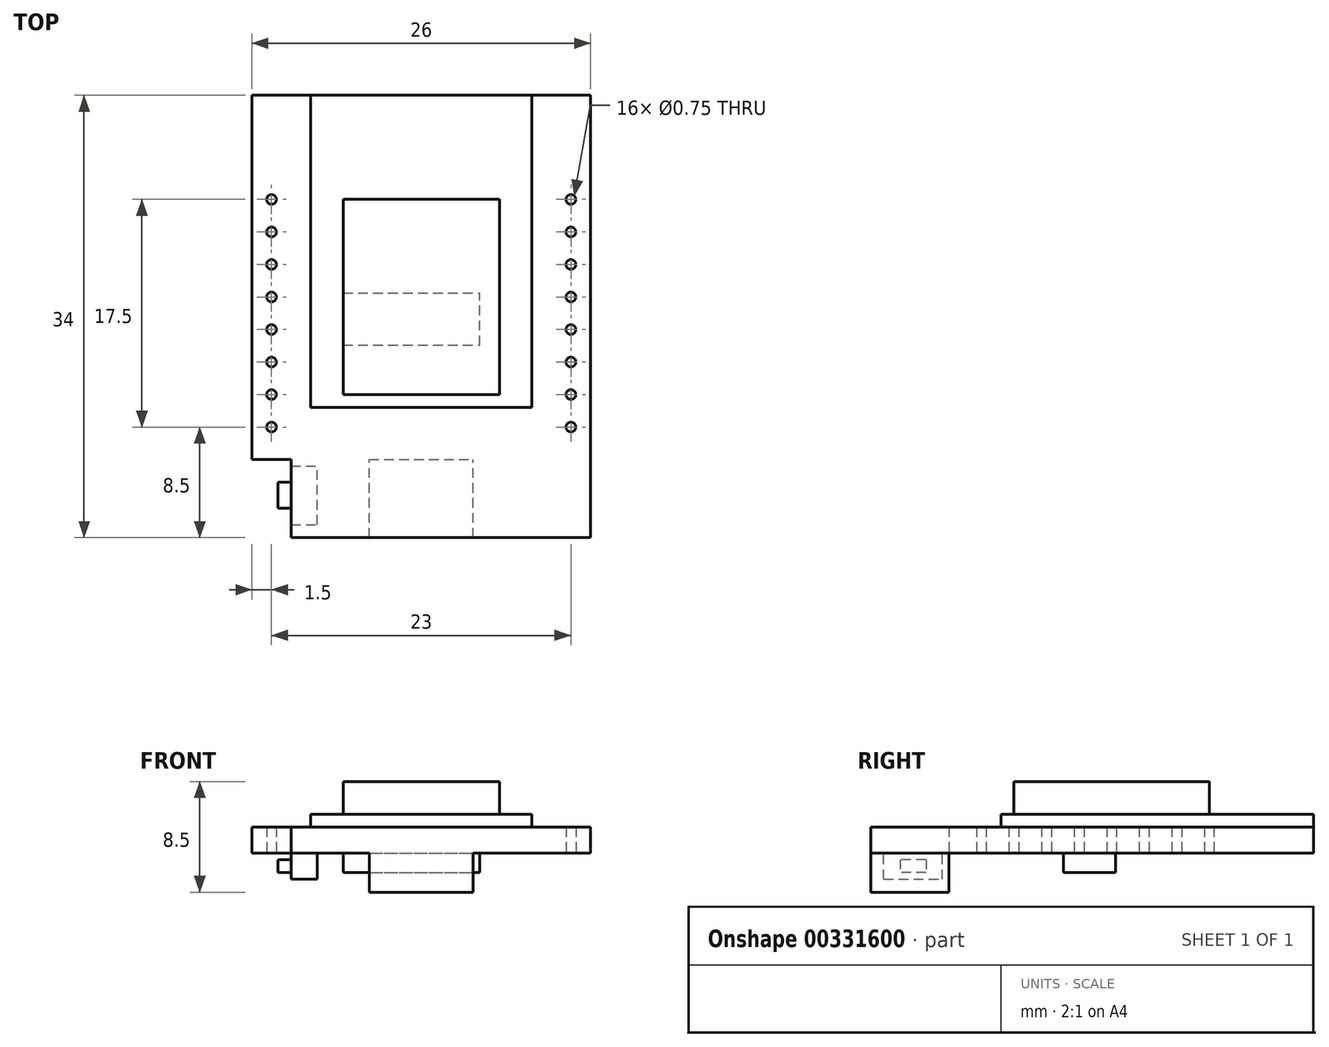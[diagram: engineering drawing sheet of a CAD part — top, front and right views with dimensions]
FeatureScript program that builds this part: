
annotation { "Feature Type Name" : "Feature", "Feature Type Description" : "" }
export const myFeature = defineFeature(function(context is Context, id is Id, definition is map)
    precondition{}
    {
        {
            var Q0;
            Q0=qCreatedBy(makeId("Top.planeOp"),FACE);
            var sketch = newSketch(context, id + "F0", { "sketchPlane" : qUnion([Q0])});
            skLineSegment(sketch, "E0.bottom", {"start": v(-13, 17) * mm, "end": v(13, 17) * mm});
            skLineSegment(sketch, "E0.top", {"start": v(-10, -17) * mm, "end": v(13, -17) * mm});
            skLineSegment(sketch, "E0.left", {"start": v(-13, 17) * mm, "end": v(-13, -11) * mm});
            skLineSegment(sketch, "E0.right", {"start": v(13, 17) * mm, "end": v(13, -17) * mm});
            skLineSegment(sketch, "E1.top", {"start": v(-13, -11) * mm, "end": v(-10, -11) * mm});
            skLineSegment(sketch, "E1.right", {"start": v(-10, -17) * mm, "end": v(-10, -11) * mm});
            skSolve(sketch);
        }
        {
            var Q0;
            Q0 = qSketchRegion(id + "F0", true);
            extrude(context, id + "F1", {"entities" : qUnion([Q0]), "depth" : 2 * mm});
        }
        {
            var Q0;
            Q0=makeQuery(id+"F1.opExtrude","CAP_FACE",FACE,{"disambiguationData":[OSD([sQuery(id+"F0.wireOp",EDGE,"E0.bottom"),sQuery(id+"F0.wireOp",EDGE,"E0.top"),sQuery(id+"F0.wireOp",EDGE,"E0.left"),sQuery(id+"F0.wireOp",EDGE,"E0.right"),sQuery(id+"F0.wireOp",EDGE,"E1.bottom"),sQuery(id+"F0.wireOp",EDGE,"E1.left")])],"isStart":false});
            var sketch = newSketch(context, id + "F2", { "sketchPlane" : qUnion([Q0])});
            skLineSegment(sketch, "E2.bottom", {"start": v(-8.5, 17) * mm, "end": v(8.5, 17) * mm});
            skLineSegment(sketch, "E2.top", {"start": v(-8.5, -7) * mm, "end": v(8.5, -7) * mm});
            skLineSegment(sketch, "E2.left", {"start": v(-8.5, 17) * mm, "end": v(-8.5, -7) * mm});
            skLineSegment(sketch, "E2.right", {"start": v(8.5, 17) * mm, "end": v(8.5, -7) * mm});
            skSolve(sketch);
        }
        {
            var Q0;
            Q0 = qSketchRegion(id + "F2", true);
            extrude(context, id + "F3", {"entities" : qUnion([Q0]), "operationType" : NewBodyOperationType.ADD, "depth" : 1 * mm});
        }
        {
            var Q0;
            Q0=makeQuery(id+"F3.opExtrude","CAP_FACE",FACE,{"disambiguationData":[OSD([sQuery(id+"F2.wireOp",EDGE,"E2.bottom"),sQuery(id+"F2.wireOp",EDGE,"E2.top"),sQuery(id+"F2.wireOp",EDGE,"E2.left"),sQuery(id+"F2.wireOp",EDGE,"E2.right")])],"isStart":false});
            var sketch = newSketch(context, id + "F4", { "sketchPlane" : qUnion([Q0])});
            skLineSegment(sketch, "E3.bottom", {"start": v(-6, 9) * mm, "end": v(6, 9) * mm});
            skLineSegment(sketch, "E3.top", {"start": v(-6, -6) * mm, "end": v(6, -6) * mm});
            skLineSegment(sketch, "E3.left", {"start": v(-6, 9) * mm, "end": v(-6, -6) * mm});
            skLineSegment(sketch, "E3.right", {"start": v(6, 9) * mm, "end": v(6, -6) * mm});
            skSolve(sketch);
        }
        {
            var Q0;
            Q0 = qSketchRegion(id + "F4", true);
            extrude(context, id + "F5", {"entities" : qUnion([Q0]), "operationType" : NewBodyOperationType.ADD, "depth" : 2.5 * mm});
        }
        {
            var Q0;
            Q0=makeQuery(id+"F1.opExtrude","CAP_FACE",FACE,{"disambiguationData":[OSD([sQuery(id+"F0.wireOp",EDGE,"E0.bottom"),sQuery(id+"F0.wireOp",EDGE,"E0.top"),sQuery(id+"F0.wireOp",EDGE,"E0.left"),sQuery(id+"F0.wireOp",EDGE,"E0.right"),sQuery(id+"F0.wireOp",EDGE,"E1.top"),sQuery(id+"F0.wireOp",EDGE,"E1.right")])],"isStart":true});
            var sketch = newSketch(context, id + "F6", { "sketchPlane" : qUnion([Q0])});
            skLineSegment(sketch, "E4.bottom", {"start": v(-4, 17) * mm, "end": v(4, 17) * mm});
            skLineSegment(sketch, "E4.top", {"start": v(-4, 11) * mm, "end": v(4, 11) * mm});
            skLineSegment(sketch, "E4.left", {"start": v(-4, 17) * mm, "end": v(-4, 11) * mm});
            skLineSegment(sketch, "E4.right", {"start": v(4, 17) * mm, "end": v(4, 11) * mm});
            skSolve(sketch);
        }
        {
            var Q0;
            Q0 = qSketchRegion(id + "F6", true);
            extrude(context, id + "F7", {"entities" : qUnion([Q0]), "operationType" : NewBodyOperationType.ADD, "depth" : 3 * mm});
        }
        {
            var Q0;
            Q0=makeQuery(id+"F1.opExtrude","CAP_FACE",FACE,{"disambiguationData":[OSD([sQuery(id+"F0.wireOp",EDGE,"E0.bottom"),sQuery(id+"F0.wireOp",EDGE,"E0.top"),sQuery(id+"F0.wireOp",EDGE,"E0.left"),sQuery(id+"F0.wireOp",EDGE,"E0.right"),sQuery(id+"F0.wireOp",EDGE,"E1.top"),sQuery(id+"F0.wireOp",EDGE,"E1.right")])],"isStart":true});
            var sketch = newSketch(context, id + "F8", { "sketchPlane" : qUnion([Q0])});
            skLineSegment(sketch, "E5.bottom", {"start": v(-10, 16) * mm, "end": v(-8, 16) * mm});
            skLineSegment(sketch, "E5.top", {"start": v(-10, 11.5) * mm, "end": v(-8, 11.5) * mm});
            skLineSegment(sketch, "E5.left", {"start": v(-10, 16) * mm, "end": v(-10, 11.5) * mm});
            skLineSegment(sketch, "E5.right", {"start": v(-8, 16) * mm, "end": v(-8, 11.5) * mm});
            skSolve(sketch);
        }
        {
            var Q0;
            Q0 = qSketchRegion(id + "F8", true);
            extrude(context, id + "F9", {"entities" : qUnion([Q0]), "operationType" : NewBodyOperationType.ADD, "depth" : 2 * mm});
        }
        {
            var Q0;
            Q0=makeQuery(id+"F9.boolean.opBoolean","MERGE",FACE,{"derivedFrom":[makeQuery(id+"F1.opExtrude","SWEPT_FACE",FACE,{"disambiguationData":[OSD([sQuery(id+"F0.wireOp",EDGE,"E1.right")])]}),makeQuery(id+"F9.opExtrude","SWEPT_FACE",FACE,{"disambiguationData":[OSD([sQuery(id+"F8.wireOp",EDGE,"E5.left")])]})]});
            var sketch = newSketch(context, id + "F10", { "sketchPlane" : qUnion([Q0])});
            skLineSegment(sketch, "E6.bottom", {"start": v(12.75, -0.5) * mm, "end": v(14.75, -0.5) * mm});
            skLineSegment(sketch, "E6.top", {"start": v(12.75, -1.5) * mm, "end": v(14.75, -1.5) * mm});
            skLineSegment(sketch, "E6.left", {"start": v(12.75, -0.5) * mm, "end": v(12.75, -1.5) * mm});
            skLineSegment(sketch, "E6.right", {"start": v(14.75, -0.5) * mm, "end": v(14.75, -1.5) * mm});
            skSolve(sketch);
        }
        {
            var Q0;
            Q0 = qSketchRegion(id + "F10", true);
            extrude(context, id + "F11", {"entities" : qUnion([Q0]), "operationType" : NewBodyOperationType.ADD, "depth" : 1 * mm});
        }
        {
            var Q0;
            Q0=makeQuery(id+"F1.opExtrude","CAP_FACE",FACE,{"disambiguationData":[OSD([sQuery(id+"F0.wireOp",EDGE,"E0.bottom"),sQuery(id+"F0.wireOp",EDGE,"E0.top"),sQuery(id+"F0.wireOp",EDGE,"E0.left"),sQuery(id+"F0.wireOp",EDGE,"E0.right"),sQuery(id+"F0.wireOp",EDGE,"E1.top"),sQuery(id+"F0.wireOp",EDGE,"E1.right")])],"isStart":true});
            var sketch = newSketch(context, id + "F12", { "sketchPlane" : qUnion([Q0])});
            skLineSegment(sketch, "E7.bottom", {"start": v(-6, 2.2) * mm, "end": v(4.5, 2.2) * mm});
            skLineSegment(sketch, "E7.top", {"start": v(-6, -1.8) * mm, "end": v(4.5, -1.8) * mm});
            skLineSegment(sketch, "E7.left", {"start": v(-6, 2.2) * mm, "end": v(-6, -1.8) * mm});
            skLineSegment(sketch, "E7.right", {"start": v(4.5, 2.2) * mm, "end": v(4.5, -1.8) * mm});
            skSolve(sketch);
        }
        {
            var Q0;
            Q0 = qSketchRegion(id + "F12", true);
            extrude(context, id + "F13", {"entities" : qUnion([Q0]), "operationType" : NewBodyOperationType.ADD, "depth" : 1.5 * mm});
        }
        {
            var Q0;
            Q0=makeQuery(id+"F1.opExtrude","CAP_FACE",FACE,{"disambiguationData":[OSD([sQuery(id+"F0.wireOp",EDGE,"E0.bottom"),sQuery(id+"F0.wireOp",EDGE,"E0.top"),sQuery(id+"F0.wireOp",EDGE,"E0.left"),sQuery(id+"F0.wireOp",EDGE,"E0.right"),sQuery(id+"F0.wireOp",EDGE,"E1.top"),sQuery(id+"F0.wireOp",EDGE,"E1.right")])],"isStart":true});
            var sketch = newSketch(context, id + "F14", { "sketchPlane" : qUnion([Q0])});
            skCircle(sketch, "E8", {"center": v(-11.5, -9) * mm, "radius": 0.38 * mm});
            skCircle(sketch, "E9.0.1.0", {"center": v(-11.5, -6.5) * mm, "radius": 0.38 * mm});
            skCircle(sketch, "E9.0.2.0", {"center": v(-11.5, -4) * mm, "radius": 0.38 * mm});
            skCircle(sketch, "E9.0.3.0", {"center": v(-11.5, -1.5) * mm, "radius": 0.38 * mm});
            skCircle(sketch, "E9.0.4.0", {"center": v(-11.5, 1) * mm, "radius": 0.38 * mm});
            skCircle(sketch, "E9.0.5.0", {"center": v(-11.5, 3.5) * mm, "radius": 0.38 * mm});
            skCircle(sketch, "E9.0.6.0", {"center": v(-11.5, 6) * mm, "radius": 0.38 * mm});
            skCircle(sketch, "E9.0.7.0", {"center": v(-11.5, 8.5) * mm, "radius": 0.38 * mm});
            skLineSegment(sketch, "E9.direction1", {"start": v(-11.5, -9) * mm, "end": v(11.5, -9) * mm, "construction": true});
            skLineSegment(sketch, "E9.direction2", {"start": v(-11.5, -9) * mm, "end": v(-11.5, -6.5) * mm, "construction": true});
            skCircle(sketch, "E10.0.1.0", {"center": v(11.5, -9) * mm, "radius": 0.38 * mm});
            skCircle(sketch, "E10.0.1.1", {"center": v(11.5, -6.5) * mm, "radius": 0.38 * mm});
            skCircle(sketch, "E10.0.1.2", {"center": v(11.5, -4) * mm, "radius": 0.38 * mm});
            skCircle(sketch, "E10.0.1.3", {"center": v(11.5, -1.5) * mm, "radius": 0.38 * mm});
            skCircle(sketch, "E10.0.1.4", {"center": v(11.5, 1) * mm, "radius": 0.38 * mm});
            skCircle(sketch, "E10.0.1.5", {"center": v(11.5, 3.5) * mm, "radius": 0.38 * mm});
            skCircle(sketch, "E10.0.1.6", {"center": v(11.5, 6) * mm, "radius": 0.38 * mm});
            skCircle(sketch, "E10.0.1.7", {"center": v(11.5, 8.5) * mm, "radius": 0.38 * mm});
            skSolve(sketch);
        }
        {
            var Q0;
            Q0 = qSketchRegion(id + "F14", true);
            extrude(context, id + "F15", {"entities" : qUnion([Q0]), "operationType" : NewBodyOperationType.REMOVE, "oppositeDirection" : true, "depth" : 25 * mm});
        }
    });
